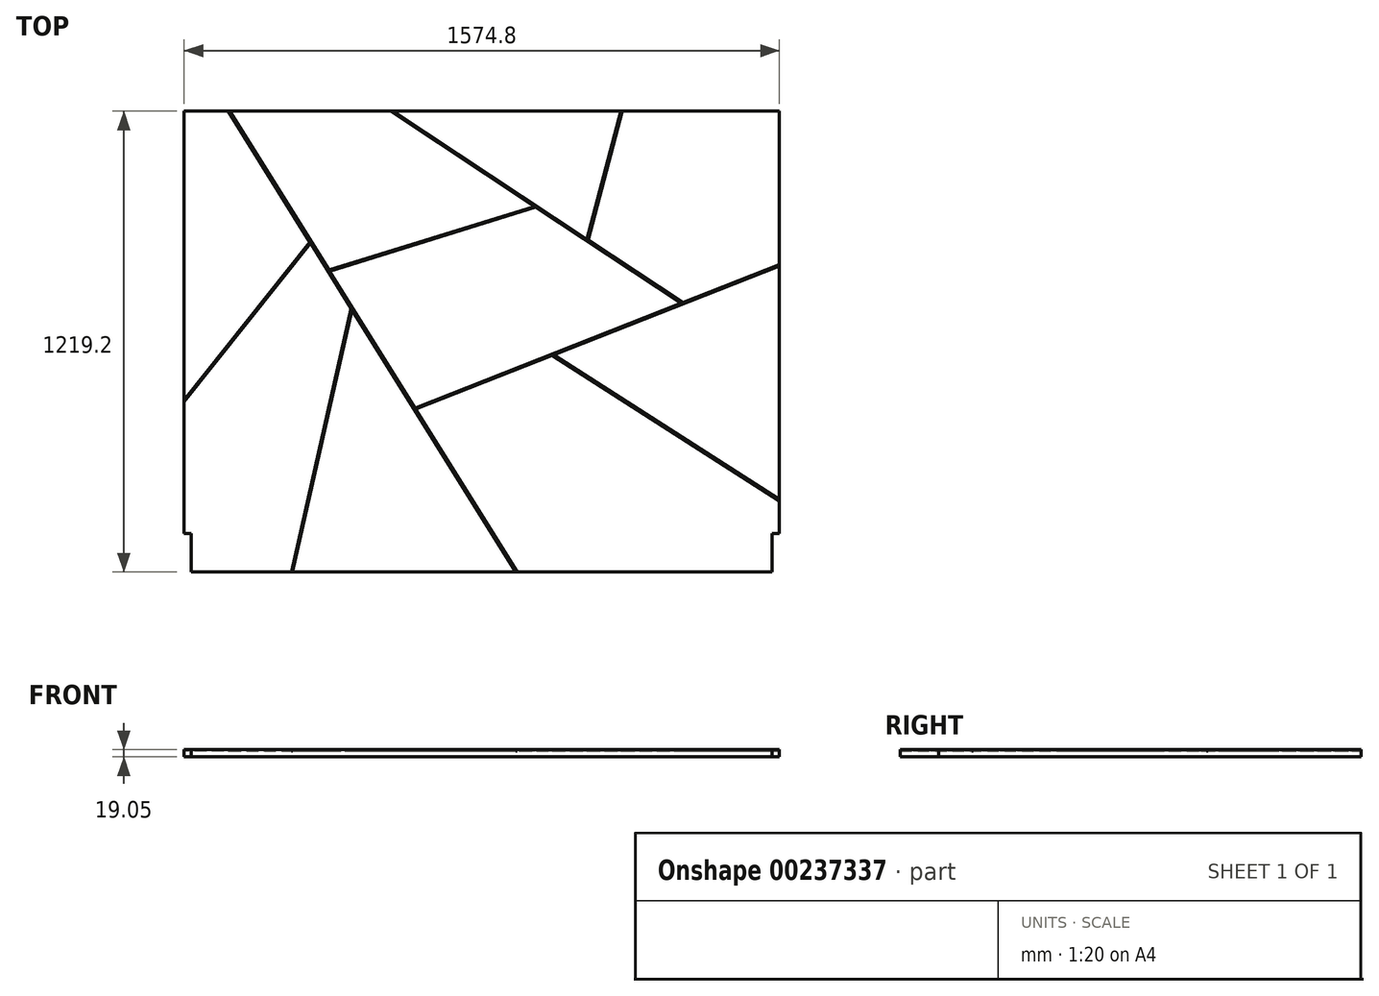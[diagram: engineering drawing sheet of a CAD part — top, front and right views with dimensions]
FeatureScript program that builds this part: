
annotation { "Feature Type Name" : "Feature", "Feature Type Description" : "" }
export const myFeature = defineFeature(function(context is Context, id is Id, definition is map)
    precondition{}
    {
        {
            var Q0;
            Q0=qCreatedBy(makeId("Top.planeOp"),FACE);
            var sketch = newSketch(context, id + "F0", { "sketchPlane" : qUnion([Q0])});
            skLineSegment(sketch, "E0.bottom", {"start": v(18.8, 0) * mm, "end": v(1555.75, 0) * mm});
            skLineSegment(sketch, "E0.top", {"start": v(0, 1219.2) * mm, "end": v(1574.8, 1219.2) * mm});
            skLineSegment(sketch, "E0.left", {"start": v(0, 101.6) * mm, "end": v(0, 1219.2) * mm});
            skLineSegment(sketch, "E0.right", {"start": v(1574.8, 101.6) * mm, "end": v(1574.8, 1219.2) * mm});
            skPoint(sketch, "E1.firstSnap0", {"position": v(0, 609.6) * mm});
            skPoint(sketch, "E1.oppositeSnap0", {"position": v(0, 609.6) * mm});
            skLineSegment(sketch, "E2.top", {"start": v(0, 101.6) * mm, "end": v(18.8, 101.6) * mm});
            skLineSegment(sketch, "E2.right", {"start": v(18.8, 0) * mm, "end": v(18.8, 101.6) * mm});
            skPoint(sketch, "E3.orphan", {"position": v(0, 0) * mm});
            skLineSegment(sketch, "E4.top", {"start": v(1574.8, 101.6) * mm, "end": v(1555.75, 101.6) * mm});
            skLineSegment(sketch, "E4.right", {"start": v(1555.75, 0) * mm, "end": v(1555.75, 101.6) * mm});
            skSolve(sketch);
        }
        {
            var Q0;
            Q0=makeQuery(id+"F0.imprint","IMPRINT",FACE,{"disambiguationData":[TD([[makeQuery(id+"F0.imprint","IMPRINT",EDGE,{"derivedFrom":sQuery(id+"F0.wireOp",EDGE,"E0.bottom")}),1.0]])]});
            extrude(context, id + "F1", {"entities" : qUnion([Q0]), "depth" : 19.05 * mm});
        }
        {
            var Q0;
            Q0=makeQuery(id+"F1.opExtrude","CAP_FACE",FACE,{"disambiguationData":[OSD([sQuery(id+"F0.wireOp",EDGE,"E0.bottom"),sQuery(id+"F0.wireOp",EDGE,"E0.top"),sQuery(id+"F0.wireOp",EDGE,"E0.left"),sQuery(id+"F0.wireOp",EDGE,"E0.right"),sQuery(id+"F0.wireOp",EDGE,"E2.top"),sQuery(id+"F0.wireOp",EDGE,"E2.right"),sQuery(id+"F0.wireOp",EDGE,"E4.top"),sQuery(id+"F0.wireOp",EDGE,"E4.right")])],"isStart":false});
            var sketch = newSketch(context, id + "F2", { "sketchPlane" : qUnion([Q0])});
            skLineSegment(sketch, "E5", {"start": v(120.25, 1219.2) * mm, "end": v(382.6, 798.7) * mm});
            skLineSegment(sketch, "E6", {"start": v(610.21, 433.87) * mm, "end": v(1315.08, 711.2) * mm});
            skLineSegment(sketch, "E7", {"start": v(1315.08, 711.2) * mm, "end": v(930.1, 965.2) * mm});
            skLineSegment(sketch, "E8", {"start": v(334.46, 869.86) * mm, "end": v(0, 449.75) * mm});
            skLineSegment(sketch, "E9", {"start": v(283.51, 0) * mm, "end": v(441.84, 697.75) * mm});
            skLineSegment(sketch, "E10", {"start": v(977.6, 575) * mm, "end": v(1574.8, 191.87) * mm});
            skLineSegment(sketch, "E11", {"start": v(384.33, 795.92) * mm, "end": v(930.1, 965.2) * mm});
            skLineSegment(sketch, "E12.0", {"start": v(117.56, 1217.52) * mm, "end": v(332.68, 872.72) * mm});
            skLineSegment(sketch, "E13.0", {"start": v(286.77, 0) * mm, "end": v(444.23, 693.92) * mm});
            skLineSegment(sketch, "E14.0", {"start": v(332.68, 872.72) * mm, "end": v(0, 454.85) * mm});
            skLineSegment(sketch, "E15.0", {"start": v(383.4, 798.95) * mm, "end": v(926.66, 967.46) * mm});
            skLineSegment(sketch, "E16.0", {"start": v(1316.83, 713.84) * mm, "end": v(1068.1, 877.95) * mm});
            skLineSegment(sketch, "E17.0", {"start": v(611.38, 430.91) * mm, "end": v(973.96, 573.57) * mm});
            skLineSegment(sketch, "E18.0", {"start": v(973.96, 573.57) * mm, "end": v(1573.09, 189.2) * mm});
            skLineSegment(sketch, "E19", {"start": v(0, 449.75) * mm, "end": v(0, 454.85) * mm});
            skLineSegment(sketch, "E20", {"start": v(283.51, 0) * mm, "end": v(286.77, 0) * mm});
            skLineSegment(sketch, "E21.trimOffspring", {"start": v(444.23, 693.92) * mm, "end": v(877.16, 0) * mm});
            skLineSegment(sketch, "E22", {"start": v(383.4, 798.95) * mm, "end": v(382.6, 798.7) * mm});
            skLineSegment(sketch, "E23.trimOffspring", {"start": v(384.33, 795.92) * mm, "end": v(880.9, 0) * mm});
            skLineSegment(sketch, "E24.trimOffspring", {"start": v(334.46, 869.86) * mm, "end": v(441.84, 697.75) * mm});
            skLineSegment(sketch, "E25.trimOffspring", {"start": v(926.66, 967.46) * mm, "end": v(545.1, 1219.2) * mm});
            skLineSegment(sketch, "E26", {"start": v(1316.83, 713.84) * mm, "end": v(1318.7, 712.61) * mm});
            skLineSegment(sketch, "E27.trimOffspring", {"start": v(1318.7, 712.61) * mm, "end": v(1574.8, 813.38) * mm});
            skLineSegment(sketch, "E28.trimOffspring", {"start": v(977.6, 575) * mm, "end": v(1574.8, 809.96) * mm});
            skLineSegment(sketch, "E29", {"start": v(1574.8, 813.38) * mm, "end": v(1574.8, 809.96) * mm});
            skLineSegment(sketch, "E30", {"start": v(545.1, 1219.2) * mm, "end": v(550.87, 1219.2) * mm});
            skLineSegment(sketch, "E31", {"start": v(117.56, 1217.52) * mm, "end": v(116.51, 1219.2) * mm});
            skLineSegment(sketch, "E32", {"start": v(116.51, 1219.2) * mm, "end": v(120.25, 1219.2) * mm});
            skLineSegment(sketch, "E33", {"start": v(880.9, 0) * mm, "end": v(877.16, 0) * mm});
            skLineSegment(sketch, "E34", {"start": v(1573.09, 189.2) * mm, "end": v(1574.8, 188.1) * mm});
            skLineSegment(sketch, "E35", {"start": v(1574.8, 188.1) * mm, "end": v(1574.8, 191.87) * mm});
            skLineSegment(sketch, "E36", {"start": v(1065.3, 879.8) * mm, "end": v(1155.47, 1219.2) * mm});
            skLineSegment(sketch, "E37", {"start": v(1068.1, 877.95) * mm, "end": v(1158.75, 1219.2) * mm});
            skLineSegment(sketch, "E38.trimOffspring", {"start": v(1065.3, 879.8) * mm, "end": v(550.87, 1219.2) * mm});
            skLineSegment(sketch, "E39", {"start": v(1155.47, 1219.2) * mm, "end": v(1158.75, 1219.2) * mm});
            skSolve(sketch);
        }
        {
            var Q0;
            Q0=makeQuery(id+"F2.imprint","IMPRINT",FACE,{"disambiguationData":[TD([[makeQuery(id+"F2.imprint","IMPRINT",EDGE,{"derivedFrom":sQuery(id+"F2.wireOp",EDGE,"E5")}),-1.0]])]});
            extrude(context, id + "F3", {"entities" : qUnion([Q0]), "operationType" : NewBodyOperationType.REMOVE, "oppositeDirection" : true, "depth" : 3.17 * mm});
        }
    });
